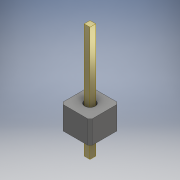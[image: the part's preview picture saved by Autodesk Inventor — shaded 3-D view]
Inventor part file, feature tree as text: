
AUTODESK INVENTOR PART (.ipt)
format: ipt  version: 2017 (Build 210142000, 142)  size: 131,072 bytes
history: native  units: mm
features: reference x5, other x3, plane x2, extrude x2, sketch x2, chamfer x1
ambient origin geometry x8: Origin, YZ Plane, XZ Plane, XY Plane, X Axis, Y Axis, Z Axis, Center Point
bodies: Solid1 (feature_tree), Solid2 (feature_tree)
feature tree (15):
  plane  "Work Plane1"
  extrude  "Extrusion1"  Depth=0.5mm
  plane  "Work Plane2"
  extrude  "Extrusion2"  Depth=2.54mm
  chamfer  "Chamfer1"  Distance=2.54mm
  sketch  "Sketch1"  dims[d0=0.5mm d1=0.5mm]
  reference  "Reference1"
  reference  "Reference2"
  sketch  "Sketch2"  dims[d2=8.0mm d3=2.0mm d4=0.0mm d5=0.0mm d6=2.54mm d7=2.54mm d8=2.0mm d9=0.0mm d10=0.2mm d11=2.0mm d12=45.0deg]
  reference  "Reference3"
  reference  "Reference4"
  reference  "Reference5"
  parser-record x1  (decoder bookkeeping rows leaked as tree rows — omitted from the tree; the rows remain in map.json)
  other  "protoswitchboard.iam"
  other  "Board:1"
note: 1 file-system path scrubbed to <path> (originals preserved in map.json)
